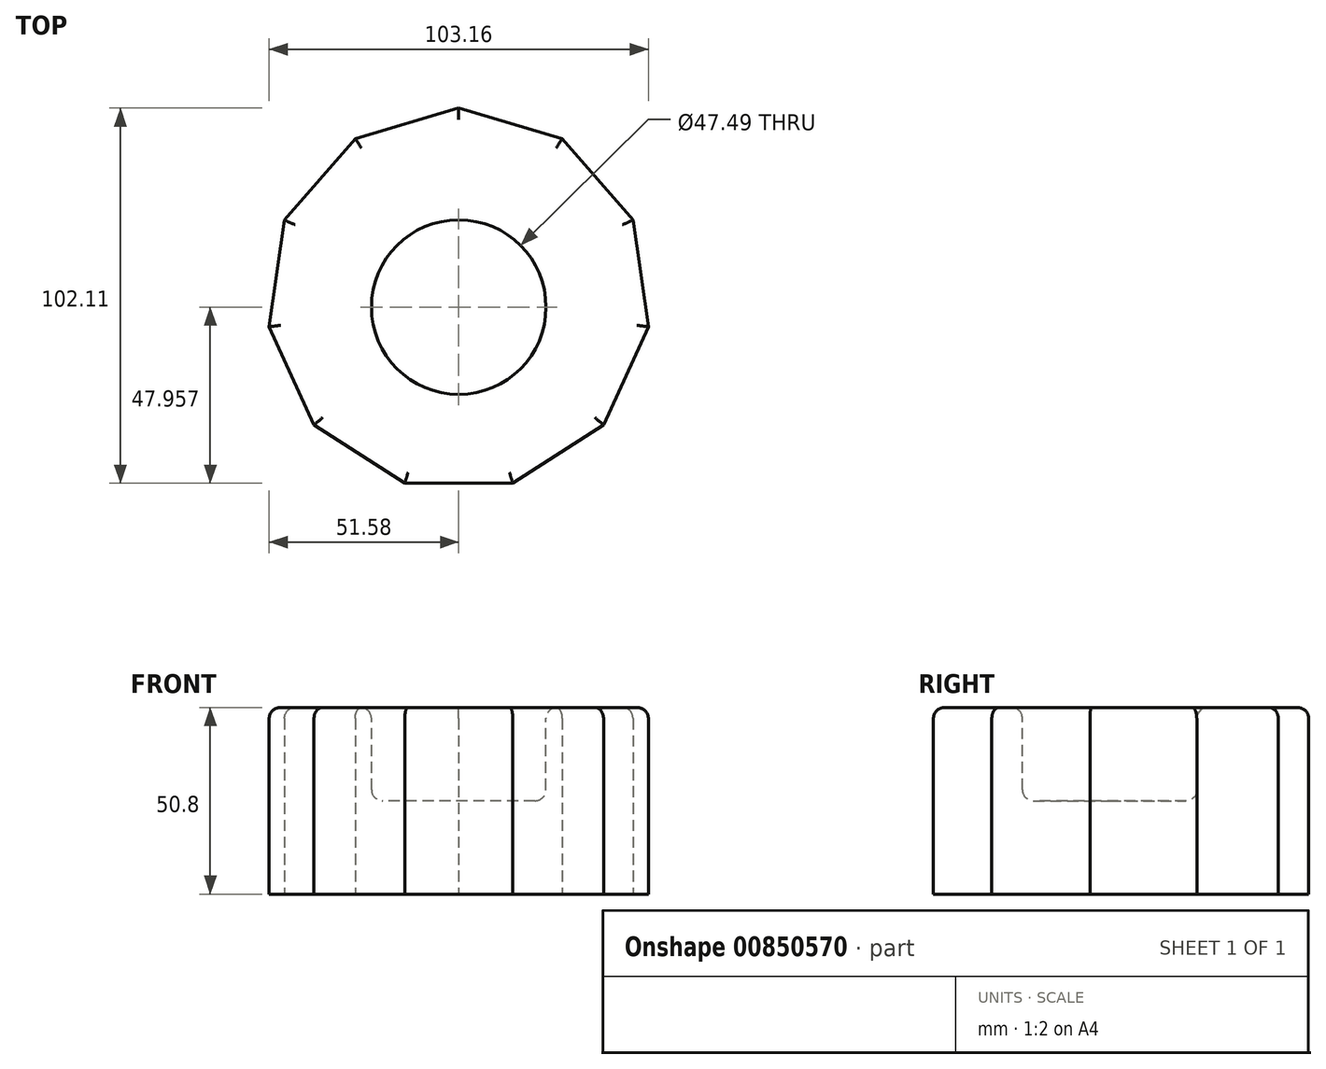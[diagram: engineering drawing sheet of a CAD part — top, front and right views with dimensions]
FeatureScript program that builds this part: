
annotation { "Feature Type Name" : "Feature", "Feature Type Description" : "" }
export const myFeature = defineFeature(function(context is Context, id is Id, definition is map)
    precondition{}
    {
        {
            var Q0;
            Q0=qCreatedBy(makeId("Top.planeOp"),FACE);
            var sketch = newSketch(context, id + "F0", { "sketchPlane" : qUnion([Q0])});
            skCircle(sketch, "E0.cCircle", {"center": v(0, 0) * mm, "radius": 50 * mm, "construction": true});
            skLineSegment(sketch, "E0.0", {"start": v(14.68, -50) * mm, "end": v(-14.68, -50) * mm});
            skLineSegment(sketch, "E0.1", {"start": v(-14.68, -50) * mm, "end": v(-39.38, -34.13) * mm});
            skLineSegment(sketch, "E0.2", {"start": v(-39.38, -34.13) * mm, "end": v(-51.58, -7.42) * mm});
            skLineSegment(sketch, "E0.3", {"start": v(-51.58, -7.42) * mm, "end": v(-47.4, 21.65) * mm});
            skLineSegment(sketch, "E0.4", {"start": v(-47.4, 21.65) * mm, "end": v(-28.17, 43.84) * mm});
            skLineSegment(sketch, "E0.5", {"start": v(-28.17, 43.84) * mm, "end": v(0, 52.11) * mm});
            skLineSegment(sketch, "E0.6", {"start": v(0, 52.11) * mm, "end": v(28.17, 43.84) * mm});
            skLineSegment(sketch, "E0.7", {"start": v(28.17, 43.84) * mm, "end": v(47.4, 21.65) * mm});
            skLineSegment(sketch, "E0.8", {"start": v(47.4, 21.65) * mm, "end": v(51.58, -7.42) * mm});
            skLineSegment(sketch, "E0.9", {"start": v(51.58, -7.42) * mm, "end": v(39.38, -34.13) * mm});
            skLineSegment(sketch, "E0.10", {"start": v(39.38, -34.13) * mm, "end": v(14.68, -50) * mm});
            skPoint(sketch, "E0.0.midPoint", {"position": v(0, -50) * mm});
            skSolve(sketch);
        }
        {
            var Q0;
            Q0=makeQuery(id+"F0.imprint","IMPRINT",FACE,{"disambiguationData":[TD([[makeQuery(id+"F0.imprint","IMPRINT",EDGE,{"derivedFrom":sQuery(id+"F0.wireOp",EDGE,"E0.0")}),-1.0]])]});
            extrude(context, id + "F1", {"entities" : qUnion([Q0]), "depth" : 50.8 * mm, "offsetDistance" : 25.4 * mm});
        }
        {
            var Q0;
            Q0=makeQuery(id+"F1.opExtrude","CAP_FACE",FACE,{"disambiguationData":[OSD([sQuery(id+"F0.wireOp",EDGE,"E0.0"),sQuery(id+"F0.wireOp",EDGE,"E0.1"),sQuery(id+"F0.wireOp",EDGE,"E0.2"),sQuery(id+"F0.wireOp",EDGE,"E0.3"),sQuery(id+"F0.wireOp",EDGE,"E0.4"),sQuery(id+"F0.wireOp",EDGE,"E0.5"),sQuery(id+"F0.wireOp",EDGE,"E0.6"),sQuery(id+"F0.wireOp",EDGE,"E0.7"),sQuery(id+"F0.wireOp",EDGE,"E0.8"),sQuery(id+"F0.wireOp",EDGE,"E0.9"),sQuery(id+"F0.wireOp",EDGE,"E0.10")])],"isStart":false});
            var sketch = newSketch(context, id + "F2", { "sketchPlane" : qUnion([Q0])});
            skCircle(sketch, "E1", {"center": v(0, -2.04) * mm, "radius": 23.75 * mm});
            skSolve(sketch);
        }
        {
            var Q0;
            Q0=makeQuery(id+"F2.imprint","IMPRINT",FACE,{"disambiguationData":[TD([[makeQuery(id+"F2.imprint","IMPRINT",EDGE,{"derivedFrom":sQuery(id+"F2.wireOp",EDGE,"E1")}),1.0]])]});
            extrude(context, id + "F3", {"entities" : qUnion([Q0]), "operationType" : NewBodyOperationType.REMOVE, "oppositeDirection" : true, "depth" : 25.4 * mm, "offsetDistance" : 25.4 * mm});
        }
        {
            var Q0;
            Q0=makeQuery(id+"F3.boolean.opBoolean","COPY",EDGE,{"derivedFrom":makeQuery(id+"F3.opExtrude","CAP_EDGE",EDGE,{"disambiguationData":[OSD([sQuery(id+"F2.wireOp",EDGE,"E1")])],"isStart":false})});
            var Q1;
            Q1=makeQuery(id+"F3.boolean.opBoolean","COPY",EDGE,{"derivedFrom":makeQuery(id+"F3.opExtrude","CAP_EDGE",EDGE,{"disambiguationData":[OSD([sQuery(id+"F2.wireOp",EDGE,"E1")])],"isStart":true})});
            var Q2;
            Q2=makeQuery(id+"F1.opExtrude","CAP_FACE",FACE,{"disambiguationData":[OSD([sQuery(id+"F0.wireOp",EDGE,"E0.0"),sQuery(id+"F0.wireOp",EDGE,"E0.1"),sQuery(id+"F0.wireOp",EDGE,"E0.2"),sQuery(id+"F0.wireOp",EDGE,"E0.3"),sQuery(id+"F0.wireOp",EDGE,"E0.4"),sQuery(id+"F0.wireOp",EDGE,"E0.5"),sQuery(id+"F0.wireOp",EDGE,"E0.6"),sQuery(id+"F0.wireOp",EDGE,"E0.7"),sQuery(id+"F0.wireOp",EDGE,"E0.8"),sQuery(id+"F0.wireOp",EDGE,"E0.9"),sQuery(id+"F0.wireOp",EDGE,"E0.10")])],"isStart":false});
            fillet(context, id + "F4", {"entities" : qUnion([Q0, Q1, Q2]), "radius" : 3 * mm, "tangentPropagation" : true, "allowEdgeOverflow" : false});
        }
    });
